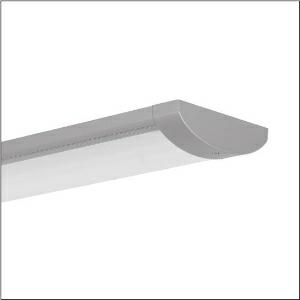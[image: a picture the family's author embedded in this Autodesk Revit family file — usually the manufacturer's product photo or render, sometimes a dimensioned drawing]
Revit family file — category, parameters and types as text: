
# Revit family: tv_20_5xa861d2n0a
name_source: partatom
category: Lighting Fixtures
units: mm (PartAtom-declared; Revit-internal decimal feet)

## family parameters
Cut with Voids When Loaded = No
Host = Face
Light Source = No
Part Type = Normal
Room Calculation Point = No
Round Connector Dimension = Use Diameter
Shared = No

## types (1)
- TV 20 (1 x LED 4000K / CRI = 80 (unbekannt), 2130 lm, 4000K)
    Apparent Load = 21 VA
    CIE Flux Codes = 48 78 95 99 100
    Color Rendering = 80
    Color Temperature = 4000K
    Default Elevation = 1800 mm
    Description = TV 20, vandal-proof luminaire, primary light control with specular reflector, of aluminium, matt, primary optical cover: enclosure, of PC, frosted, light emission: direct distribution, primary light characteristic: symmetric, installation type: surface-mounted, LED, rated luminous flux: 2.130lm, luminous efficacy: 101lm/W, light colour: 840, colour temperature: 4000K, control gear: DALI, mains connection: 230V, AC, 50Hz, rated input power: 21W, luminaire housing, of aluminium, coated, Siteco® metallic grey (DB 702S), with wall and ceiling fixing element, length: 705mm, width: 260mm, height: 70mm, mounting height: 2.5..4.0m, protection rating (complete): IP65, insulation class (complete): insulation class I (protective earthing), certification: CE, protection symbol: F, impact resistance: 2x IK10, standard: EN 60598, packaging unit: 1 piece
    Height = 70 mm
    Lamp = 1 x LED 4000K / CRI >= 80 (unbekannt)
    Lamp Light Flux = 2130 lm
    Lamp count = 1
    Length = 705 mm
    Luminous efficacy = 101 lm/W
    Manufacturer = Siteco
    ModVariant = No
    Model = 5XA861D2N0A
    Mounting Place = Ceiling
    Mounting Type = Surface mounted
    Number of Poles = 1
    OnlyDefault = Yes
    Power Factor = 1
    Product Name = TV 20
    Product group = vandal-proof luminaire
    ProductGroupID = 310
    Protection Class = Protection class I
    Protection Degree = IP 65
    RLX_Detail_Level = 1
    RLX_Emergency_Light_Flux = 0 lm
    RLX_Emergency_Type = 0
    RLX_Emergency_Type_DB = No
    RlxData = <blob elided: 34213 chars, md5=38b9aa3f>
    Socket = socket
    Standby Power = 0 W
    System Light Flux = 2130 lm
    System Power = 21 W
    Type Comments = Product without accessories
    Type Image = l_1004809.jpg
    URL = http://relux.com
    VarID = ---
    Voltage = 0 V
    Weight = 0.00 kg
    Width = 260 mm

## geometry (parser evidence)
native form markers: Blend x4, Sweep x11
no freeform markers — native parametric forms only
